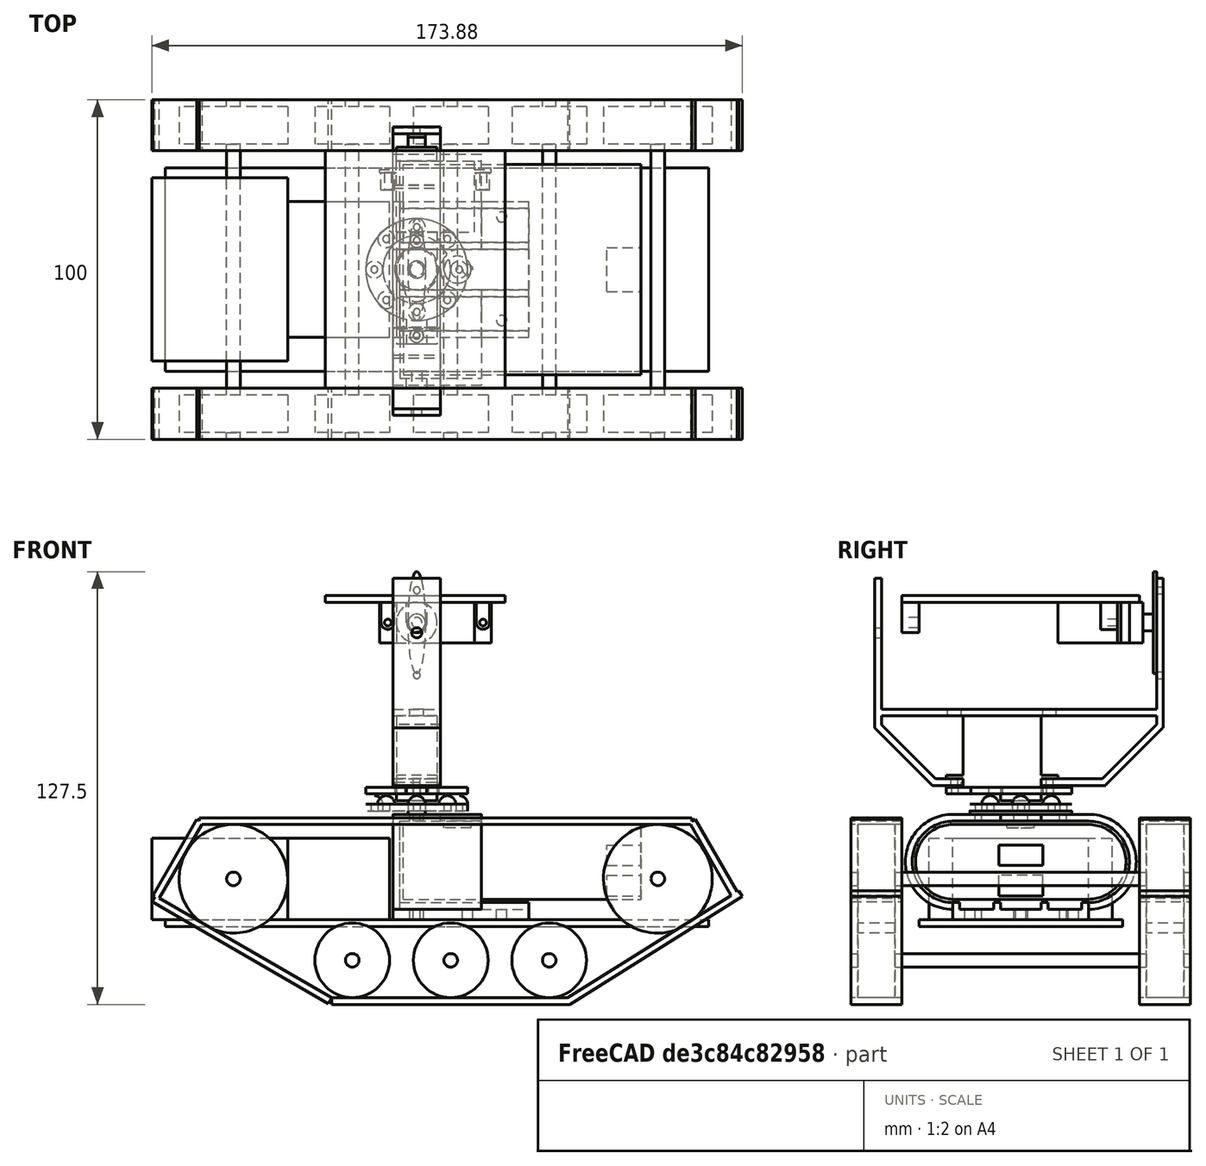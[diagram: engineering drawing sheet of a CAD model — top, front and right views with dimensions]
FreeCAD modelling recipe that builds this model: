
FCSTD DOCUMENT
Label: androidtank_7
License: CC-BY 3.0
LicenseURL: http://creativecommons.org/licenses/by/3.0/
objects: Part::Cylinder×55, Part::Box×36, Part::MultiFuse×25, Part::Sphere×8, Part::Cut×7, Part::FeaturePython×1, App::DocumentObjectGroup×1
note: 132 computed .brp shape members not serialized (recipe doc carries the construction recipe); baked Part::Feature solids carry a one-line shape summary decoded from their .brp

FEATURE [Part::Box] Box  label="MainFrame"
  Height = 2
  Length = 160
  Width = 60
FEATURE [Part::Box] Box001001  label="Moter Unit2"
  Height = 24
  Length = 30
  Placement = pos=(36,10,2) rot=(0,0,1;0rad)
  Width = 40
FEATURE [Part::Cylinder] Cylinder  label="Shaft"
  Angle = 360
  Height = 100
  Placement = pos=(20,-20,14) rot=(-1,0,0;1.5708rad)
  Radius = 2
FEATURE [Part::Box] Box001002
  Height = 2
  Length = 145
  Placement = pos=(10,-20,30) rot=(0,0,1;0rad)
  Width = 15
FEATURE [Part::Box] Box001002001
  Height = 2
  Length = 70
  Placement = pos=(49,-20,-23) rot=(0,0,1;0rad)
  Width = 15
FEATURE [Part::Box] Box001002001001
  Height = 2
  Length = 60
  Placement = pos=(119,-20,-23) rot=(0,-1,0;0.558505rad)
  Width = 15
FEATURE [Part::Box] Box001002001002
  Height = 2
  Length = 60
  Placement = pos=(49,-20,-21) rot=(0,1,0;3.66519rad)
  Width = 15
FEATURE [Part::Box] Box001002001003
  Height = 2
  Length = 26
  Placement = pos=(-2,-20,8) rot=(0,-1,0;1.0472rad)
  Width = 15
FEATURE [Part::Box] Box001002001003001
  Height = 2
  Length = 26
  Placement = pos=(169,-20,9) rot=(0,-1,0;2.0944rad)
  Width = 15
FEATURE [Part::MultiFuse] Fusion002001002  label="Caterpiller1"
  Shapes = -> [Box001002,Box001002001,Box001002001002,Box001002001001,Box001002001003,Box001002001003001]
FEATURE [Part::MultiFuse] Fusion002001002001  label="Caterpiller2"
  Placement = pos=(0,85,0) rot=(0,0,1;0rad)
  Shapes = -> [Box001002,Box001002001,Box001002001002,Box001002001001,Box001002001003,Box001002001003001]
FEATURE [Part::Cylinder] Cylinder002001001002  label="Wheel006"
  Angle = 360
  Height = 11
  Placement = pos=(20,78,14) rot=(1,0,0;1.5708rad)
  Radius = 11
FEATURE [Part::Cylinder] Cylinder002001001002001  label="Wheel007"
  Angle = 360
  Height = 11
  Placement = pos=(20,-7,14) rot=(1,0,0;1.5708rad)
  Radius = 11
FEATURE [Part::Cylinder] Cylinder002001002001  label="Shaft002"
  Angle = 360
  Height = 100
  Placement = pos=(20,-20,14) rot=(-1,0,0;1.5708rad)
  Radius = 2
FEATURE [Part::MultiFuse] Fusion002001002002002  label="SWheelSet1"
  Placement = pos=(35,0,-24) rot=(0,0,1;0rad)
  Shapes = -> [Cylinder002001002001,Cylinder002001001002,Cylinder002001001002001]
FEATURE [Part::MultiFuse] Fusion002001002002002001  label="SWheelSet2"
  Placement = pos=(64,0,-24) rot=(0,0,1;0rad)
  Shapes = -> [Cylinder002001002001,Cylinder002001001002,Cylinder002001001002001]
FEATURE [Part::MultiFuse] Fusion002001002002002001001  label="SWheelSet3"
  Placement = pos=(93,0,-24) rot=(0,0,1;0rad)
  Shapes = -> [Cylinder002001002001,Cylinder002001001002,Cylinder002001001002001]
FEATURE [Part::Box] Box001002001003002
  Height = 22
  Length = 70
  Placement = pos=(0,0,-11) rot=(0,0,1;0rad)
  Width = 40
FEATURE [Part::Cylinder] Cylinder002001001002002
  Angle = 360
  Height = 70
  Placement = pos=(0,0,0) rot=(0,1,0;1.5708rad)
  Radius = 11
FEATURE [Part::Cylinder] Cylinder001
  Angle = 360
  Height = 70
  Placement = pos=(0,40,0) rot=(0,1,0;1.5708rad)
  Radius = 11
FEATURE [Part::Cylinder] Cylinder002001001002003  label="PowerButton"
  Angle = 360
  Height = 2
  Placement = pos=(16,20,10) rot=(0,0,1;0rad)
  Radius = 4
FEATURE [Part::Box] Box001002001003003  label="USB1"
  Height = 6
  Length = 15
  Placement = pos=(60,13.5,-1) rot=(0,0,1;0rad)
  Width = 13
FEATURE [Part::Box] Box001001001  label="USB2"
  Height = 6
  Length = 15
  Placement = pos=(60,13.5,-10) rot=(0,0,1;0rad)
  Width = 13
FEATURE [Part::MultiFuse] Fusion002001002002002001002
  Shapes = -> [Cylinder001,Box001002001003002,Cylinder002001001002002]
FEATURE [Part::MultiFuse] Fusion001001
  Shapes = -> [Box001001001,Cylinder002001001002003,Box001002001003003]
FEATURE [Part::Cut] Cut  label="Eneloop"
  Base = -> Fusion002001002002002001002
  Placement = pos=(70,10,19) rot=(0,0,1;0rad)
  Tool = -> Fusion001001
FEATURE [Part::Cylinder] Cylinder001001  label="Cylinder002"
  Angle = 360
  Height = 26
  Placement = pos=(0,50,19) rot=(0,1,0;1.5708rad)
  Radius = 14
FEATURE [Part::Box] Box001002001003002001  label="Box001002001003002001001001001006001001002001003001006"
  Height = 28
  Length = 26
  Placement = pos=(0,10,5) rot=(0,0,1;0rad)
  Width = 40
FEATURE [Part::Cylinder] Cylinder002001001002002001  label="Cylinder003"
  Angle = 360
  Height = 26
  Placement = pos=(0,10,19) rot=(0,1,0;1.5708rad)
  Radius = 14
FEATURE [Part::Box] Box001  label="Moter Unit1"
  Height = 24
  Length = 40
  Placement = pos=(-4,3,2) rot=(0,0,1;0rad)
  Width = 54
FEATURE [Part::Box] Box001002001003002001001  label="Box003"
  Height = 5
  Length = 40
  Placement = pos=(0,10,2) rot=(0,0,1;0rad)
  Width = 40
FEATURE [Part::Box] Box001002001003002001002  label="Box004"
  Height = 24
  Length = 26
  Placement = pos=(2,10,7) rot=(0,0,1;0rad)
  Width = 40
FEATURE [Part::Cylinder] Cylinder001001001  label="Cylinder004"
  Angle = 360
  Height = 26
  Placement = pos=(2,50,19) rot=(0,1,0;1.5708rad)
  Radius = 12
FEATURE [Part::Cylinder] Cylinder002001001002002001001  label="Cylinder005"
  Angle = 360
  Height = 26
  Placement = pos=(2,10,19) rot=(0,1,0;1.5708rad)
  Radius = 12
FEATURE [Part::Cylinder] Cylinder002001001002003001  label="PowerButton001"
  Angle = 360
  Height = 4
  Placement = pos=(20,30,30) rot=(0,0,1;0rad)
  Radius = 6
FEATURE [Part::Box] Box001002001003002001003  label="Box005"
  Height = 4
  Length = 10
  Placement = pos=(20,24,30) rot=(0,0,1;0rad)
  Width = 12
FEATURE [Part::Box] Box001002001003002001001001  label="Box006"
  Height = 3
  Length = 40
  Placement = pos=(2,12,5) rot=(0,0,1;0rad)
  Width = 10
FEATURE [Part::Box] Box001002001003002001001001001  label="Box007"
  Height = 3
  Length = 40
  Placement = pos=(2,24,5) rot=(0,0,1;0rad)
  Width = 12
FEATURE [Part::Box] Box001002001003002001001001001001  label="Box008"
  Height = 3
  Length = 40
  Placement = pos=(2,38,5) rot=(0,0,1;0rad)
  Width = 10
FEATURE [Part::MultiFuse] Fusion002001002002002001003
  Shapes = -> [Box001002001003002001,Cylinder001001,Cylinder002001001002002001,Box001002001003002001001]
FEATURE [Part::MultiFuse] Fusion002001002002002001004
  Shapes = -> [Box001002001003002001002,Cylinder002001001002002001001,Cylinder001001001,Box001002001003002001001001001001,Box001002001003002001001001001,Box001002001003002001001001,Box001002001003002001003,Cylinder002001001002003001]
FEATURE [Part::Cut] Cut001  label="BatteryFrame"
  Base = -> Fusion002001002002002001003
  Placement = pos=(67,0,0) rot=(0,0,1;0rad)
  Tool = -> Fusion002001002002002001004
FEATURE [Part::Cylinder] Cylinder002001001002002001002001  label="Cylinder007"
  Angle = 360
  Height = 40
  Placement = pos=(74,17.5,0) rot=(0,0,1;0rad)
  Radius = 1
FEATURE [Part::Cylinder] Cylinder002001001002002001002  label="Cylinder006"
  Angle = 360
  Height = 40
  Placement = pos=(74,42.5,0) rot=(0,0,1;0rad)
  Radius = 1
FEATURE [Part::Cylinder] Cylinder002001001002002001002001001  label="Cylinder008"
  Angle = 360
  Height = 40
  Placement = pos=(89,30,0) rot=(0,0,1;0rad)
  Radius = 1.5
FEATURE [Part::Cylinder] Cylinder002001001002002001002001002  label="Cylinder009"
  Angle = 360
  Height = 40
  Placement = pos=(99,45.5,0) rot=(0,0,1;0rad)
  Radius = 1.5
FEATURE [Part::Cylinder] Cylinder002001001002002001002001003  label="Cylinder0010"
  Angle = 360
  Height = 40
  Placement = pos=(99,15,0) rot=(0,0,1;0rad)
  Radius = 1.5
FEATURE [Part::Box] Box001002001003002001001001001006  label="Box009"
  Height = 2
  Length = 53
  Placement = pos=(47,-5,100) rot=(0,0,1;0rad)
  Width = 70
FEATURE [Part::Box] Box001002001003002001001001001006001  label="Box010"
  Height = 44
  Length = 14
  Placement = pos=(67,70,66) rot=(0,0,1;0rad)
  Width = 2
FEATURE [Part::Box] Box001002001003002001001001001006001001  label="Box011"
  Height = 2
  Length = 13
  Placement = pos=(67.5,12.5,48) rot=(0,0,1;0rad)
  Width = 23.5
FEATURE [Part::Box] Box001002001003002001001001001006001001001  label="Box012"
  Height = 44
  Length = 14
  Placement = pos=(67,-13,66) rot=(0,0,1;0rad)
  Width = 2
FEATURE [Part::Cylinder] Cylinder002001001002002001002001008  label="Hole1"
  Angle = 360
  Height = 20
  Placement = pos=(74,-20,94) rot=(-1,0,0;1.5708rad)
  Radius = 1.5
FEATURE [Part::Cylinder] Cylinder002001001002002001002001008001  label="Hole2"
  Angle = 360
  Height = 20
  Placement = pos=(74,60,106.5) rot=(-1,0,0;1.5708rad)
  Radius = 1
FEATURE [Part::Cylinder] Cylinder002001001002002001002001008001001  label="Hole4"
  Angle = 360
  Height = 20
  Placement = pos=(74,38.5,41) rot=(0,0,1;0rad)
  Radius = 1
FEATURE [Part::Cylinder] Cylinder002001001002002001002001008001001001  label="Hole3"
  Angle = 360
  Height = 20
  Placement = pos=(74,60,81.5) rot=(-1,0,0;1.5708rad)
  Radius = 1
FEATURE [Part::Cylinder] Cylinder002001001002002001002001008001001002  label="Hole5"
  Angle = 360
  Height = 20
  Placement = pos=(74,10.5,41) rot=(0,0,1;0rad)
  Radius = 1
FEATURE [Part::Box] Box001002001003002001001001001006001001001001  label="Box013"
  Height = 24
  Length = 14
  Placement = pos=(67,4,49) rot=(1,0,0;0.785397rad)
  Width = 2
FEATURE [Part::Box] Box001002001003002001001001001006001001001001001  label="Box014"
  Height = 24
  Length = 14
  Placement = pos=(67,53.41,50.41) rot=(-1,0,0;0.785397rad)
  Width = 2
FEATURE [Part::Box] Box001002001003002001001001001006001001002001  label="Box016"
  Height = 2
  Length = 14
  Placement = pos=(67,4,49) rot=(0,0,1;0rad)
  Width = 9
FEATURE [Part::Box] Box001002001003002001001001001006001001002001001  label="Box017"
  Height = 2
  Length = 14
  Placement = pos=(67,36,49) rot=(0,0,1;0rad)
  Width = 19
FEATURE [Part::Box] Box001002001003002001001001001006001001002001002  label="Box015"
  Height = 2
  Length = 14
  Placement = pos=(67,-13,69.5) rot=(0,0,1;0rad)
  Width = 85
FEATURE [Part::MultiFuse] Fusion002001002002002001009
  Shapes = -> [Box001002001003002001001001001006001,Box001002001003002001001001001006001001001001,Box001002001003002001001001001006001001001,Box001002001003002001001001001006001001001001001,Box001002001003002001001001001006001001002001,Box001002001003002001001001001006001001002001002,Box001002001003002001001001001006001001002001001]
FEATURE [Part::Cylinder] Cylinder002001001002002001002001008001001002001  label="Hole006"
  Angle = 360
  Height = 20
  Placement = pos=(74,10.5,60) rot=(0,0,1;0rad)
  Radius = 2
FEATURE [Part::Cylinder] Cylinder002001001002002001002001008001001002002  label="Hole007"
  Angle = 360
  Height = 20
  Placement = pos=(74,38.5,60) rot=(0,0,1;0rad)
  Radius = 2
FEATURE [Part::MultiFuse] Fusion002001002002002001010
  Shapes = -> [Cylinder002001001002002001002001008001,Box001002001003002001001001001006001001,Cylinder002001001002002001002001008001001,Cylinder002001001002002001002001008,Cylinder002001001002002001002001008001001001,Cylinder002001001002002001002001008001001002,Cylinder002001001002002001002001008001001002002,Cylinder002001001002002001002001008001001002001]
FEATURE [Part::Cut] Cut003  label="HeadFrame"
  Base = -> Fusion002001002002002001009
  Placement = pos=(0,0,-7.5) rot=(0,0,1;0rad)
  Tool = -> Fusion002001002002002001010
FEATURE [Part::Cylinder] Cylinder002001001002002001002001008001001002003  label="Cylinder025"
  Angle = 360
  Height = 5
  Placement = pos=(74,0,94) rot=(1,0,0;1.5708rad)
  Radius = 3
FEATURE [Part::Box] Box001002001003002001001001001006001001002001003  label="Box020"
  Height = 6
  Length = 6
  Placement = pos=(71,-5,94) rot=(0,0,1;0rad)
  Width = 5
FEATURE [Part::Cylinder] Cylinder002001001002002001002001008001001002003001  label="Cylinder026"
  Angle = 360
  Height = 7
  Placement = pos=(74,1,94) rot=(1,0,0;1.5708rad)
  Radius = 1.5
FEATURE [Part::Box] Box001002001003002001001001001006001001002001003001001  label="Box022"
  Height = 6
  Length = 4
  Placement = pos=(91.5,53.5,94) rot=(0,0,1;0rad)
  Width = 5
FEATURE [Part::Cylinder] Cylinder002001001002002001002001008001001002003002  label="Cylinder027"
  Angle = 360
  Height = 5
  Placement = pos=(65.5,58.5,94) rot=(1,0,0;1.5708rad)
  Radius = 2
FEATURE [Part::Cylinder] Cylinder002001001002002001002001008001001002003002001  label="Cylinder028"
  Angle = 360
  Height = 5
  Placement = pos=(93.5,58.5,94) rot=(1,0,0;1.5708rad)
  Radius = 2
FEATURE [Part::Box] Box001002001003002001001001001006001001002001003001  label="Box021"
  Height = 6
  Length = 4
  Placement = pos=(63.5,53.5,94) rot=(0,0,1;0rad)
  Width = 5
FEATURE [Part::Cylinder] Cylinder002001001002002001002001008001001002003002002  label="Cylinder029"
  Angle = 360
  Height = 6
  Placement = pos=(65.5,59,94) rot=(1,0,0;1.5708rad)
  Radius = 1
FEATURE [Part::Cylinder] Cylinder002001001002002001002001008001001002003002001001  label="Cylinder030"
  Angle = 360
  Height = 6
  Placement = pos=(93.5,59,94) rot=(1,0,0;1.5708rad)
  Radius = 1
FEATURE [Part::MultiFuse] Fusion002001002002002001011
  Shapes = -> [Box001002001003002001001001001006,Box001002001003002001001001001006001001002001003001001,Cylinder002001001002002001002001008001001002003002001,Box001002001003002001001001001006001001002001003,Cylinder002001001002002001002001008001001002003,Box001002001003002001001001001006001001002001003001,Cylinder002001001002002001002001008001001002003002]
FEATURE [Part::MultiFuse] Fusion002001002002002001012
  Shapes = -> [Cylinder002001001002002001002001008001001002003001,Cylinder002001001002002001002001008001001002003002002,Cylinder002001001002002001002001008001001002003002001001]
FEATURE [Part::Cut] Cut002003  label="HeadMount"
  Base = -> Fusion002001002002002001011
  Placement = pos=(0,0,-4.5) rot=(0,0,1;0rad)
  Tool = -> Fusion002001002002002001012
FEATURE [Part::Cylinder] Cylinder002001001002002001002001001001  label="Cylinder040"
  Angle = 360
  Height = 40
  Placement = pos=(74,30,0) rot=(0,0,1;0rad)
  Radius = 2
FEATURE [Part::MultiFuse] Fusion002001002002002001013  label="BatteryFrameHoles"
  Shapes = -> [Cylinder002001001002002001002001,Cylinder002001001002002001002,Cylinder002001001002002001002001001,Cylinder002001001002002001002001002,Cylinder002001001002002001002001003,Cylinder002001001002002001002001001001]
FEATURE [Part::Cut] Cut002004  label="BatteryFrame2"
  Base = -> Cut001
  Tool = -> Fusion002001002002002001013
FEATURE [Part::Box] Box001002001003002001001001001006001001002001003001002  label="ServoBody"
  Height = 21
  Length = 23
  Width = 12
FEATURE [Part::Cylinder] Cylinder002001001002002001002001008001001002003002001002  label="ServoBody2"
  Angle = 360
  Height = 4
  Placement = pos=(6,6,21) rot=(0,0,1;0rad)
  Radius = 6
FEATURE [Part::Box] Box001002001003002001001001001006001001002001003001003  label="ServoBody3"
  Height = 1
  Length = 33
  Placement = pos=(-5,0,17.5) rot=(0,0,1;0rad)
  Width = 12
FEATURE [Part::Cylinder] Cylinder001001002  label="ServoAxis"
  Angle = 360
  Height = 4
  Placement = pos=(6,6,24) rot=(0,0,1;0rad)
  Radius = 2.5
FEATURE [Part::MultiFuse] Fusion005  label="ServoArmL"
  Shapes = -> [Cylinder001001002,Box001002001003002001001001001006001001002001003001003,Box001002001003002001001001001006001001002001003001002,Cylinder002001001002002001002001008001001002003002001002]
FEATURE [Part::MultiFuse] Fusion006  label="ServoYaw"
  Placement = pos=(80,36,62) rot=(0.707107,-0.707107,0;3.14159rad)
  Shapes = -> [Fusion005]
FEATURE [Part::Cylinder] Cylinder003001001004  label="Cylinder002001001002002001002001008001001002003002001006"
  Angle = 360
  Height = 0.5
  Placement = pos=(-2.5,6,20.5) rot=(0,0,1;0rad)
  Radius = 2
FEATURE [Part::Cylinder] Cylinder003001001005  label="Cylinder011"
  Angle = 360
  Height = 2
  Placement = pos=(6,6,21) rot=(0,0,1;0rad)
  Radius = 15
FEATURE [Part::Cylinder] Cylinder003001001004001  label="Cylinder010"
  Angle = 360
  Height = 0.5
  Placement = pos=(25.5,6,20.5) rot=(0,0,1;0rad)
  Radius = 2
FEATURE [Part::Cylinder] Cylinder003001001005001  label="Cylinder012"
  Angle = 360
  Height = 2
  Placement = pos=(6,6,21) rot=(0,0,1;0rad)
  Radius = 6.5
FEATURE [Part::Cylinder] Cylinder003001001005001001  label="Cylinder013"
  Angle = 360
  Height = 2
  Placement = pos=(12,6,21) rot=(0,0,1;0rad)
  Radius = 3.5
FEATURE [Part::Box] Box002
  Height = 2
  Length = 10
  Placement = pos=(18,3,21) rot=(0,0,1;0rad)
  Width = 6
FEATURE [Part::Cylinder] Cylinder003001001004002  label="Cylinder014"
  Angle = 360
  Height = 5
  Placement = pos=(-2.5,6,19.5) rot=(0,0,1;0rad)
  Radius = 1
FEATURE [Part::Cylinder] Cylinder003001001004001001  label="Cylinder015"
  Angle = 360
  Height = 5
  Placement = pos=(25.5,6,19.5) rot=(0,0,1;0rad)
  Radius = 1
FEATURE [Part::MultiFuse] Fusion008
  Shapes = -> [Cylinder003001001005,Box002,Cylinder003001001004,Cylinder003001001004001]
FEATURE [Part::MultiFuse] Fusion009
  Shapes = -> [Cylinder003001001005001,Cylinder003001001005001001,Cylinder003001001004002,Cylinder003001001004001001]
FEATURE [Part::Cut] Cut002  label="Guide1"
  Base = -> Fusion008
  Placement = pos=(80,36,62) rot=(-0.705662,0.708549,0;3.14159rad)
  Tool = -> Fusion009
FEATURE [Part::Box] Box001002001003002001001001001006001001002001003001004  label="ServoBody004"
  Height = 21
  Length = 23
  Width = 12
FEATURE [Part::Cylinder] Cylinder002001001002002001002001008001001002003002001003  label="ServoBody005"
  Angle = 360
  Height = 4
  Placement = pos=(6,6,21) rot=(0,0,1;0rad)
  Radius = 6
FEATURE [Part::Box] Box001002001003002001001001001006001001002001003001005  label="ServoBody006"
  Height = 1
  Length = 33
  Placement = pos=(-5,0,17.5) rot=(0,0,1;0rad)
  Width = 12
FEATURE [Part::Cylinder] Cylinder001001003  label="ServoAxis001"
  Angle = 360
  Height = 4
  Placement = pos=(6,6,24) rot=(0,0,1;0rad)
  Radius = 2.5
FEATURE [Part::MultiFuse] Fusion005001  label="ServoArmL001"
  Shapes = -> [Cylinder001001003,Box001002001003002001001001001006001001002001003001005,Box001002001003002001001001001006001001002001003001004,Cylinder002001001002002001002001008001001002003002001003]
FEATURE [Part::Cylinder] Cylinder002001001002002001002001008001001002003002001004  label="Cylinder002001001002002001002001008001001002003002001012"
  Angle = 360
  Height = 2
  Radius = 2.5
FEATURE [Part::FeaturePython] Scale  # Draft clone (typed FeaturePython)
  Objects = -> [Cylinder002001001002002001002001008001001002003002001004]
  Placement = pos=(0,0,1) rot=(0,0,1;0rad)
  Scale = (6,1,0.5)
FEATURE [Part::MultiFuse] Fusion  label="Arm"
  Placement = pos=(6,6,27) rot=(0,0,1;1.5708rad)
  Shapes = -> [Cylinder002001001002002001002001008001001002003002001004,Scale]
FEATURE [Part::MultiFuse] Fusion006001  label="ServoPitch"
  Placement = pos=(68,41,95.5) rot=(-1,0,0;1.5708rad)
  Shapes = -> [Fusion005001,Fusion]
FEATURE [Part::Cylinder] Cylinder002001001002002001002001008001001002003002001005  label="Wheel1"
  Angle = 360
  Height = 11
  Placement = pos=(20,78,14) rot=(1,0,0;1.5708rad)
  Radius = 16
FEATURE [Part::Cylinder] Cylinder002001001002002001002001008001001002003002001005001  label="Wheel2"
  Angle = 360
  Height = 11
  Placement = pos=(20,-7,14) rot=(1,0,0;1.5708rad)
  Radius = 16
FEATURE [Part::MultiFuse] Fusion002001002002002001014  label="LWheelSet1"
  Shapes = -> [Cylinder,Cylinder002001001002002001002001008001001002003002001005,Cylinder002001001002002001002001008001001002003002001005001]
FEATURE [Part::MultiFuse] Fusion002001002002002001014001  label="LWheelSet2"
  Placement = pos=(125,0,0) rot=(0,0,1;0rad)
  Shapes = -> [Cylinder,Cylinder002001001002002001002001008001001002003002001005,Cylinder002001001002002001002001008001001002003002001005001]
FEATURE [App::DocumentObjectGroup] ____________  label="DriveFrame"
  Group = -> [Box,Box001,Box001001,Fusion002001002,Fusion002001002001,Fusion002001002002002,Fusion002001002002002001,Fusion002001002002002001001,Fusion002001002002002001014,Fusion002001002002002001014001]
FEATURE [Part::Cylinder] Cylinder003001001003  label="Cylinder002001001002002001002001008001001002003002001013"
  Angle = 360
  Height = 2
  Placement = pos=(6,6,26) rot=(0,0,1;0rad)
  Radius = 15
FEATURE [Part::Sphere] Sphere
  Angle1 = -90
  Angle2 = 0
  Angle3 = 360
  Placement = pos=(-3,-3,26) rot=(0,0,1;0rad)
  Radius = 2.5
FEATURE [Part::Sphere] Sphere001
  Angle1 = -90
  Angle2 = 0
  Angle3 = 360
  Placement = pos=(15,-3,26) rot=(0,0,1;0rad)
  Radius = 2.5
FEATURE [Part::Sphere] Sphere001001  label="Sphere002"
  Angle1 = -90
  Angle2 = 0
  Angle3 = 360
  Placement = pos=(15,15,26) rot=(0,0,1;0rad)
  Radius = 2.5
FEATURE [Part::Sphere] Sphere001001001  label="Sphere003"
  Angle1 = -90
  Angle2 = 0
  Angle3 = 360
  Placement = pos=(-3,15,26) rot=(0,0,1;0rad)
  Radius = 2.5
FEATURE [Part::Cylinder] Cylinder003001001005001004  label="Cylinder020"
  Angle = 360
  Height = 4
  Placement = pos=(-6.5,6,26) rot=(0,0,1;0rad)
  Radius = 1
FEATURE [Part::Cylinder] Cylinder003001001001003  label="Cylinder021"
  Angle = 360
  Height = 4
  Placement = pos=(18.5,6,26) rot=(0,0,1;0rad)
  Radius = 1
FEATURE [Part::Cylinder] Cylinder003001001005001003001  label="Cylinder022"
  Angle = 360
  Height = 5
  Placement = pos=(-3,-3,26) rot=(0,0,1;0rad)
  Radius = 1
FEATURE [Part::Cylinder] Cylinder003001001001002001  label="Cylinder023"
  Angle = 360
  Height = 5
  Placement = pos=(15,-3,26) rot=(0,0,1;0rad)
  Radius = 1
FEATURE [Part::Sphere] Sphere001001001001  label="Sphere004"
  Angle1 = -90
  Angle2 = 0
  Angle3 = 360
  Placement = pos=(-6.5,6,26) rot=(0,0,1;0rad)
  Radius = 2.5
FEATURE [Part::Sphere] Sphere001001001001001  label="Sphere005"
  Angle1 = -90
  Angle2 = 0
  Angle3 = 360
  Placement = pos=(18.5,6,26) rot=(0,0,1;0rad)
  Radius = 2.5
FEATURE [Part::Sphere] Sphere001001001001001001  label="Sphere006"
  Angle1 = -90
  Angle2 = 0
  Angle3 = 360
  Placement = pos=(6,-6.5,26) rot=(0,0,1;0rad)
  Radius = 2.5
FEATURE [Part::Sphere] Sphere001001001001001001001  label="Sphere007"
  Angle1 = -90
  Angle2 = 0
  Angle3 = 360
  Placement = pos=(6,18.5,26) rot=(0,0,1;0rad)
  Radius = 2.5
FEATURE [Part::Cylinder] Cylinder003001001003001  label="Cylinder024"
  Angle = 360
  Height = 2
  Placement = pos=(6,6,26) rot=(0,0,1;0rad)
  Radius = 10
FEATURE [Part::MultiFuse] Fusion014
  Shapes = -> [Sphere,Cylinder003001001003,Sphere001001001,Sphere001001001001001001,Sphere001001001001,Sphere001,Sphere001001,Sphere001001001001001001001,Sphere001001001001001]
FEATURE [Part::Cylinder] Cylinder003001001005001003001001  label="Cylinder002001001002002001002001008001001002003002001014"
  Angle = 360
  Height = 5
  Placement = pos=(-3,15,26) rot=(0,0,1;0rad)
  Radius = 1
FEATURE [Part::Cylinder] Cylinder003001001001002001001  label="Cylinder002001001002002001002001008001001002003002001015"
  Angle = 360
  Height = 5
  Placement = pos=(15,15,26) rot=(0,0,1;0rad)
  Radius = 1
FEATURE [Part::Cylinder] Cylinder003001001005001003001001001  label="Cylinder002001001002002001002001008001001002003002001016"
  Angle = 360
  Height = 5
  Placement = pos=(6,18.5,26) rot=(0,0,1;0rad)
  Radius = 1
FEATURE [Part::Cylinder] Cylinder003001001005001003001001001001  label="Cylinder002001001002002001002001008001001002003002001017"
  Angle = 360
  Height = 5
  Placement = pos=(6,-6.5,26) rot=(0,0,1;0rad)
  Radius = 1
FEATURE [Part::MultiFuse] Fusion015
  Shapes = -> [Cylinder003001001003001,Cylinder003001001005001004,Cylinder003001001001003,Cylinder003001001005001003001,Cylinder003001001001002001,Cylinder003001001005001003001001,Cylinder003001001005001003001001001001,Cylinder003001001001002001001,Cylinder003001001005001003001001001]
FEATURE [Part::Cut] Cut002005  label="Guide2"
  Base = -> Fusion014
  Placement = pos=(68,36,62) rot=(1,0,0;3.14159rad)
  Tool = -> Fusion015
